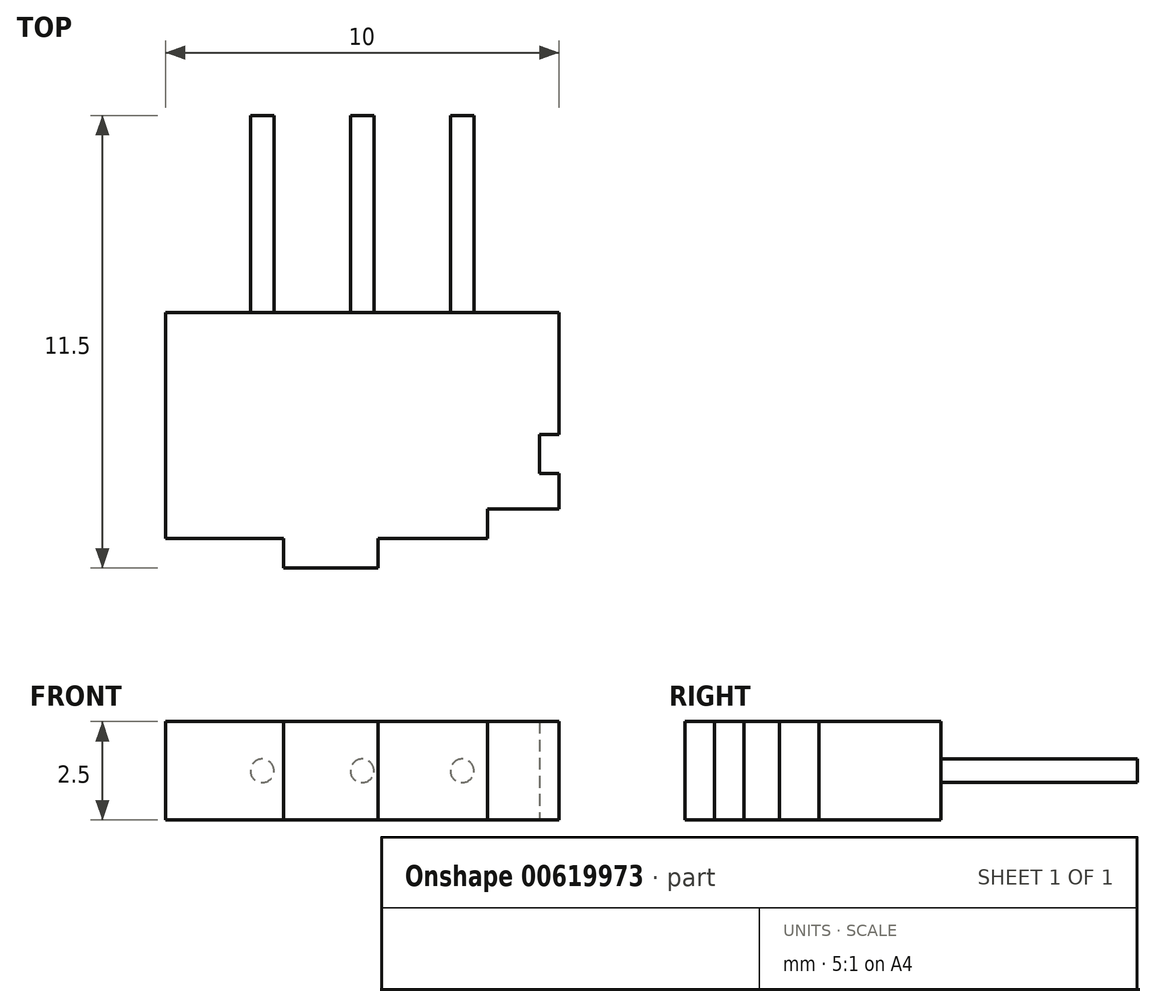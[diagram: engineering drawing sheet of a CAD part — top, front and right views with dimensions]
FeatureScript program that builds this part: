
annotation { "Feature Type Name" : "Feature", "Feature Type Description" : "" }
export const myFeature = defineFeature(function(context is Context, id is Id, definition is map)
    precondition{}
    {
        {
            var Q0;
            Q0=qCreatedBy(makeId("Top.planeOp"),FACE);
            var sketch = newSketch(context, id + "F0", { "sketchPlane" : qUnion([Q0])});
            skLineSegment(sketch, "E0.bottom", {"start": v(5, 2.5) * mm, "end": v(-5, 2.5) * mm});
            skLineSegment(sketch, "E0.top", {"start": v(5, -2.5) * mm, "end": v(-5, -2.5) * mm});
            skLineSegment(sketch, "E0.left", {"start": v(5, 2.5) * mm, "end": v(5, -0.6) * mm});
            skLineSegment(sketch, "E0.right", {"start": v(-5, 2.5) * mm, "end": v(-5, -2.5) * mm});
            skPoint(sketch, "E0.middle", {"position": v(0, 0) * mm});
            skLineSegment(sketch, "E1.bottom", {"start": v(5, -0.6) * mm, "end": v(4.5, -0.6) * mm});
            skLineSegment(sketch, "E1.top", {"start": v(5, -1.6) * mm, "end": v(4.5, -1.6) * mm});
            skLineSegment(sketch, "E1.right", {"start": v(4.5, -0.6) * mm, "end": v(4.5, -1.6) * mm});
            skLineSegment(sketch, "E2.trimOffspring", {"start": v(5, -1.6) * mm, "end": v(5, -2.5) * mm});
            skSolve(sketch);
        }
        {
            var Q0;
            Q0 = qSketchRegion(id + "F0", true);
            extrude(context, id + "F1", {"entities" : qUnion([Q0]), "depth" : 2.5 * mm, "offsetDistance" : 25 * mm});
        }
        {
            var Q0;
            Q0=makeQuery(id+"F1.opExtrude","SWEPT_FACE",FACE,{"disambiguationData":[OSD([sQuery(id+"F0.wireOp",EDGE,"E0.top")])]});
            var sketch = newSketch(context, id + "F2", { "sketchPlane" : qUnion([Q0])});
            skLineSegment(sketch, "E3.bottom", {"start": v(-5, 2.5) * mm, "end": v(3.19, 2.5) * mm});
            skLineSegment(sketch, "E3.top", {"start": v(-5, 0) * mm, "end": v(3.19, 0) * mm});
            skLineSegment(sketch, "E3.left", {"start": v(-5, 2.5) * mm, "end": v(-5, 0) * mm});
            skLineSegment(sketch, "E3.right", {"start": v(3.19, 2.5) * mm, "end": v(3.19, 0) * mm});
            skSolve(sketch);
        }
        {
            var Q0;
            Q0 = qSketchRegion(id + "F2", true);
            extrude(context, id + "F3", {"entities" : qUnion([Q0]), "operationType" : NewBodyOperationType.ADD, "depth" : 0.75 * mm, "offsetDistance" : 25 * mm});
        }
        {
            var Q0;
            Q0=makeQuery(id+"F3.opExtrude","CAP_FACE",FACE,{"disambiguationData":[OSD([sQuery(id+"F2.wireOp",EDGE,"E3.bottom"),sQuery(id+"F2.wireOp",EDGE,"E3.top"),sQuery(id+"F2.wireOp",EDGE,"E3.left"),sQuery(id+"F2.wireOp",EDGE,"E3.right")])],"isStart":false});
            var sketch = newSketch(context, id + "F4", { "sketchPlane" : qUnion([Q0])});
            skLineSegment(sketch, "E4.bottom", {"start": v(-2, 2.5) * mm, "end": v(0.4, 2.5) * mm});
            skLineSegment(sketch, "E4.top", {"start": v(-2, 0) * mm, "end": v(0.4, 0) * mm});
            skLineSegment(sketch, "E4.left", {"start": v(-2, 2.5) * mm, "end": v(-2, 0) * mm});
            skLineSegment(sketch, "E4.right", {"start": v(0.4, 2.5) * mm, "end": v(0.4, 0) * mm});
            skLineSegment(sketch, "E5", {"start": v(-0.8, 2.5) * mm, "end": v(-0.8, 0) * mm});
            skSolve(sketch);
        }
        {
            var Q0;
            Q0 = qSketchRegion(id + "F4", true);
            extrude(context, id + "F5", {"entities" : qUnion([Q0]), "operationType" : NewBodyOperationType.ADD, "depth" : 0.75 * mm, "offsetDistance" : 25 * mm});
        }
        {
            var Q0;
            Q0=makeQuery(id+"F1.opExtrude","SWEPT_FACE",FACE,{"disambiguationData":[OSD([sQuery(id+"F0.wireOp",EDGE,"E0.bottom")])]});
            var sketch = newSketch(context, id + "F6", { "sketchPlane" : qUnion([Q0])});
            skCircle(sketch, "E6", {"center": v(2.54, 1.25) * mm, "radius": 0.3 * mm});
            skPoint(sketch, "E6.centerSnap0", {"position": v(5, 1.25) * mm});
            skCircle(sketch, "E7", {"center": v(0, 1.25) * mm, "radius": 0.3 * mm});
            skCircle(sketch, "E8", {"center": v(-2.54, 1.25) * mm, "radius": 0.3 * mm});
            skSolve(sketch);
        }
        {
            var Q0;
            Q0 = qSketchRegion(id + "F6", true);
            extrude(context, id + "F7", {"entities" : qUnion([Q0]), "operationType" : NewBodyOperationType.ADD, "depth" : 5 * mm, "offsetDistance" : 25 * mm});
        }
    });
